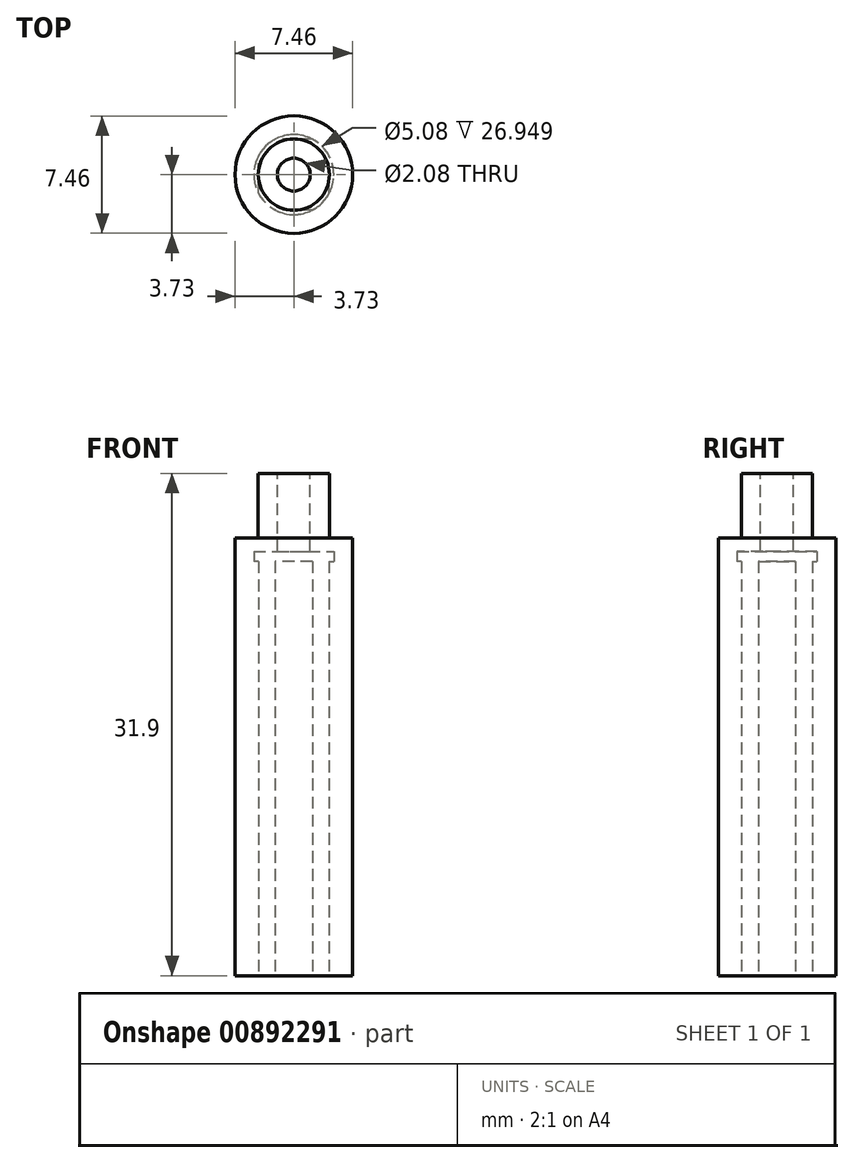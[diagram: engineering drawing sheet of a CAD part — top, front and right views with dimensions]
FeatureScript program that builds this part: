
annotation { "Feature Type Name" : "Feature", "Feature Type Description" : "" }
export const myFeature = defineFeature(function(context is Context, id is Id, definition is map)
    precondition{}
    {
        {
            var Q0;
            Q0=qCreatedBy(makeId("Top.planeOp"),FACE);
            var sketch = newSketch(context, id + "F0", { "sketchPlane" : qUnion([Q0])});
            skCircle(sketch, "E0", {"center": v(0, 0) * mm, "radius": 3.73 * mm});
            skSolve(sketch);
        }
        {
            var Q0;
            Q0=qSketchRegion(id+"F0",true);
            extrude(context, id + "F1", {"entities" : qUnion([Q0]), "depth" : 27.8 * mm, "offsetDistance" : 25.4 * mm});
        }
        {
            var Q0;
            Q0=makeQuery(id+"F1.opExtrude","CAP_FACE",FACE,{"disambiguationData":[OSD([sQuery(id+"F0.wireOp",EDGE,"E0")])],"isStart":false});
            var sketch = newSketch(context, id + "F2", { "sketchPlane" : qUnion([Q0])});
            skCircle(sketch, "E1", {"center": v(0, 0) * mm, "radius": 2.26 * mm});
            skSolve(sketch);
        }
        {
            var Q0;
            Q0=qSketchRegion(id+"F2",true);
            extrude(context, id + "F3", {"entities" : qUnion([Q0]), "operationType" : NewBodyOperationType.ADD, "depth" : 4.1 * mm, "offsetDistance" : 25.4 * mm});
        }
        {
            var Q0;
            Q0=makeQuery(id+"F3.opExtrude","CAP_FACE",FACE,{"disambiguationData":[OSD([sQuery(id+"F2.wireOp",EDGE,"E1")])],"isStart":false});
            var sketch = newSketch(context, id + "F4", { "sketchPlane" : qUnion([Q0])});
            skCircle(sketch, "E2", {"center": v(0, 0) * mm, "radius": 1.04 * mm});
            skSolve(sketch);
        }
        {
            var Q0;
            Q0=qSketchRegion(id+"F4",true);
            extrude(context, id + "F5", {"entities" : qUnion([Q0]), "operationType" : NewBodyOperationType.REMOVE, "oppositeDirection" : true, "depth" : 47.02 * mm, "offsetDistance" : 25.4 * mm});
        }
        {
            var Q0;
            Q0=makeQuery(id+"F1.opExtrude","CAP_FACE",FACE,{"disambiguationData":[OSD([sQuery(id+"F0.wireOp",EDGE,"E0")])],"isStart":true});
            var sketch = newSketch(context, id + "F6", { "sketchPlane" : qUnion([Q0])});
            skCircle(sketch, "E3", {"center": v(0, 0) * mm, "radius": 2.54 * mm});
            skSolve(sketch);
        }
        {
            var Q0;
            Q0=qSketchRegion(id+"F6",true);
            extrude(context, id + "F7", {"entities" : qUnion([Q0]), "operationType" : NewBodyOperationType.REMOVE, "oppositeDirection" : true, "depth" : 26.95 * mm, "offsetDistance" : 25.4 * mm});
        }
        {
            var Q0;
            Q0=makeQuery(id+"F1.opExtrude","CAP_FACE",FACE,{"disambiguationData":[OSD([sQuery(id+"F0.wireOp",EDGE,"E0")])],"isStart":true});
            var sketch = newSketch(context, id + "F8", { "sketchPlane" : qUnion([Q0])});
            skLineSegment(sketch, "E4.bottom", {"start": v(2.25, 2.25) * mm, "end": v(-2.25, 2.25) * mm});
            skLineSegment(sketch, "E4.top", {"start": v(2.25, -2.25) * mm, "end": v(-2.25, -2.25) * mm});
            skLineSegment(sketch, "E4.left", {"start": v(2.25, 2.25) * mm, "end": v(2.25, -2.25) * mm});
            skLineSegment(sketch, "E4.right", {"start": v(-2.25, 2.25) * mm, "end": v(-2.25, -2.25) * mm});
            skPoint(sketch, "E4.middle", {"position": v(0, 0) * mm});
            skSolve(sketch);
        }
        {
            var Q0;
            {var subQ0=sQuery(id+"F8.wireOp",EDGE,"E4.bottom");var subQ1=makeQuery(id+"F7.boolean.opBoolean","COPY",EDGE,{"derivedFrom":makeQuery(id+"F7.opExtrude","CAP_EDGE",EDGE,{"disambiguationData":[OSD([sQuery(id+"F6.wireOp",EDGE,"E3")])],"isStart":true})});var subQ2=makeQuery(id+"F8.imprint","INTERSECT",VERTEX,{"disambiguationData":[OD(0.0)],"derivedFrom":[subQ1,subQ0]});Q0=makeQuery(id+"F8.imprint","IMPRINT",FACE,{"disambiguationData":[TD([[makeQuery(id+"F8.imprint","IMPRINT",EDGE,{"disambiguationData":[TD([[subQ2,-1.0]])],"derivedFrom":subQ0}),-1.0]])]});}
            var Q1;
            {var subQ0=sQuery(id+"F8.wireOp",EDGE,"E4.right");var subQ1=makeQuery(id+"F7.boolean.opBoolean","COPY",EDGE,{"derivedFrom":makeQuery(id+"F7.opExtrude","CAP_EDGE",EDGE,{"disambiguationData":[OSD([sQuery(id+"F6.wireOp",EDGE,"E3")])],"isStart":true})});var subQ2=makeQuery(id+"F8.imprint","INTERSECT",VERTEX,{"disambiguationData":[OD(0.0)],"derivedFrom":[subQ1,subQ0]});Q1=makeQuery(id+"F8.imprint","IMPRINT",FACE,{"disambiguationData":[TD([[makeQuery(id+"F8.imprint","IMPRINT",EDGE,{"disambiguationData":[TD([[subQ2,-1.0]])],"derivedFrom":subQ0}),-1.0]])]});}
            var Q2;
            {var subQ0=sQuery(id+"F8.wireOp",EDGE,"E4.top");var subQ1=makeQuery(id+"F7.boolean.opBoolean","COPY",EDGE,{"derivedFrom":makeQuery(id+"F7.opExtrude","CAP_EDGE",EDGE,{"disambiguationData":[OSD([sQuery(id+"F6.wireOp",EDGE,"E3")])],"isStart":true})});var subQ2=makeQuery(id+"F8.imprint","INTERSECT",VERTEX,{"disambiguationData":[OD(0.0)],"derivedFrom":[subQ1,subQ0]});Q2=makeQuery(id+"F8.imprint","IMPRINT",FACE,{"disambiguationData":[TD([[makeQuery(id+"F8.imprint","IMPRINT",EDGE,{"disambiguationData":[TD([[subQ2,-1.0]])],"derivedFrom":subQ0}),1.0]])]});}
            var Q3;
            {var subQ0=sQuery(id+"F8.wireOp",EDGE,"E4.left");var subQ1=makeQuery(id+"F7.boolean.opBoolean","COPY",EDGE,{"derivedFrom":makeQuery(id+"F7.opExtrude","CAP_EDGE",EDGE,{"disambiguationData":[OSD([sQuery(id+"F6.wireOp",EDGE,"E3")])],"isStart":true})});var subQ2=makeQuery(id+"F8.imprint","INTERSECT",VERTEX,{"disambiguationData":[OD(0.0)],"derivedFrom":[subQ1,subQ0]});Q3=makeQuery(id+"F8.imprint","IMPRINT",FACE,{"disambiguationData":[TD([[makeQuery(id+"F8.imprint","IMPRINT",EDGE,{"disambiguationData":[TD([[subQ2,-1.0]])],"derivedFrom":subQ0}),1.0]])]});}
            extrude(context, id + "F9", {"entities" : qUnion([Q0, Q1, Q2, Q3]), "operationType" : NewBodyOperationType.ADD, "oppositeDirection" : true, "depth" : 26.3 * mm, "offsetDistance" : 25.4 * mm});
        }
    });
